# Revit family: S-752
name_source: partatom
category: Plumbing Fixtures
revit_build: Autodesk Revit 2015 (Build: 20140606_1530(x64)
units: mm (PartAtom-declared; Revit-internal decimal feet)

## types (6) — shared parameters
B = 52 mm
Description = CHANNEL GRID, SOFT, FOR CHANNELS WIDTH 50
Grid = INOX AISI304
Manufacturer = Jimten
Material = INOX AISI304
Model = S-752
Total Minimum Height = 8 mm
Type Comments = GRID TO BE FILLED IN WITH THE SAME FLOOR FINISHING THAN THE SHOWER FLOOR
URL = http://www.jimten.com

## per-type parameters (varying)
| type | A | Reference | Size |
| 50x350mm_SOFT | 340 mm  [stored 1.11549 ft] | 13535 | 350mm x 50mm |
| 50x550mm_SOFT | 540 mm  [stored 1.77165 ft] | 13555 | 550mm x 50mm |
| 50x650mm_SOFT | 640 mm  [stored 2.09974 ft] | 13565 | 650mm x 50mm |
| 50x750mm_SOFT | 740 mm  [stored 2.42782 ft] | 13575 | 750mm x 50mm |
| 50x850mm_SOFT | 840 mm  [stored 2.75591 ft] | 13585 | 850mm x 50mm |
| 50x950mm_SOFT | 940 mm  [stored 3.08399 ft] | 13595 | 950mm x 50mm |

note: [stored X ft] marks values corroborated as IEEE doubles in the binary element streams (Revit-internal decimal feet)

## geometry (parser evidence)
native form markers: Blend x3, Sweep x3
no freeform markers — native parametric forms only
